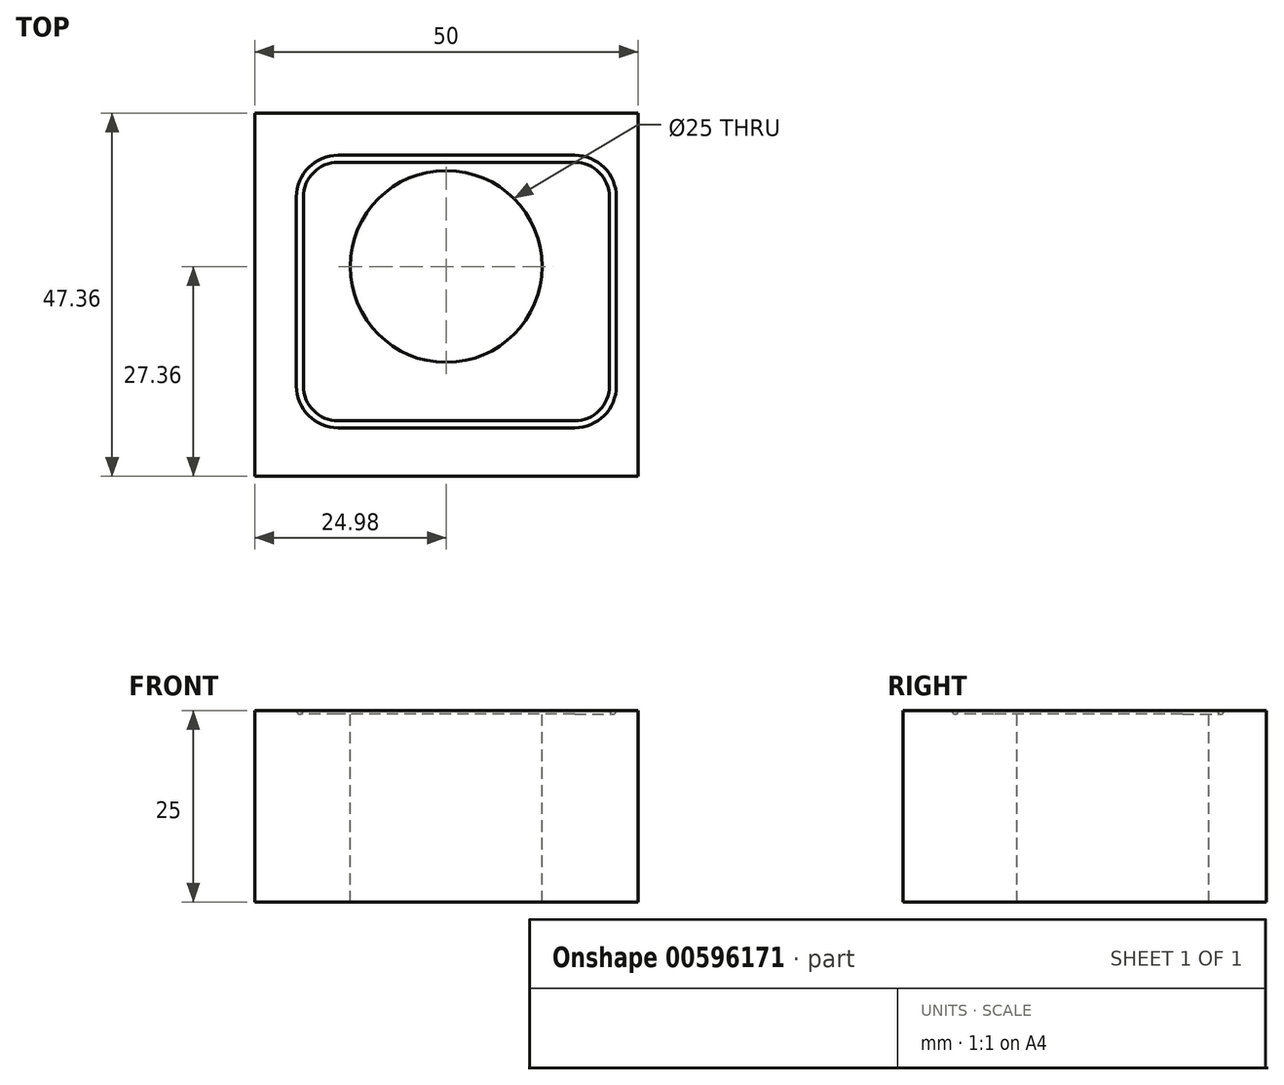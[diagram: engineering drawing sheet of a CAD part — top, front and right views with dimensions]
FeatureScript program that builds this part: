
annotation { "Feature Type Name" : "Feature", "Feature Type Description" : "" }
export const myFeature = defineFeature(function(context is Context, id is Id, definition is map)
    precondition{}
    {
        {
            var Q0;
            Q0=qCreatedBy(makeId("Top.planeOp"),FACE);
            var sketch = newSketch(context, id + "F0", { "sketchPlane" : qUnion([Q0])});
            skLineSegment(sketch, "E0.bottom", {"start": v(-24.98, 20) * mm, "end": v(25.02, 20) * mm});
            skLineSegment(sketch, "E0.top", {"start": v(-24.98, -27.36) * mm, "end": v(25.02, -27.36) * mm});
            skLineSegment(sketch, "E0.left", {"start": v(-24.98, 20) * mm, "end": v(-24.98, -27.36) * mm});
            skLineSegment(sketch, "E0.right", {"start": v(25.02, 20) * mm, "end": v(25.02, -27.36) * mm});
            skSolve(sketch);
        }
        {
            var Q0;
            Q0=makeQuery(id+"F0.imprint","IMPRINT",FACE,{"disambiguationData":[TD([[makeQuery(id+"F0.imprint","IMPRINT",EDGE,{"derivedFrom":sQuery(id+"F0.wireOp",EDGE,"E0.bottom")}),-1.0]])]});
            var Q1;
            Q1 = qBodyType(qCreatedBy(id + "F0" ,EDGE), BodyType.WIRE);
            var Q2;
            Q2=sQuery(id+"F0.wireOp",EDGE,"E0.right");
            extrude(context, id + "F1", {"entities" : qUnion([Q0]), "surfaceEntities" : qUnion([Q1, Q2]), "depth" : 25 * mm, "offsetDistance" : 25 * mm});
        }
        {
            var Q0;
            Q0=makeQuery(id+"F1.opExtrude","CAP_FACE",FACE,{"disambiguationData":[OSD([sQuery(id+"F0.wireOp",EDGE,"E0.bottom"),sQuery(id+"F0.wireOp",EDGE,"E0.top"),sQuery(id+"F0.wireOp",EDGE,"E0.left"),sQuery(id+"F0.wireOp",EDGE,"E0.right")])],"isStart":false});
            var sketch = newSketch(context, id + "F2", { "sketchPlane" : qUnion([Q0])});
            skCircle(sketch, "E1", {"center": v(0, 0) * mm, "radius": 12.5 * mm});
            skSolve(sketch);
        }
        {
            var Q0;
            Q0=makeQuery(id+"F2.imprint","IMPRINT",FACE,{"disambiguationData":[TD([[makeQuery(id+"F2.imprint","IMPRINT",EDGE,{"derivedFrom":sQuery(id+"F2.wireOp",EDGE,"E1")}),1.0]])]});
            var Q1;
            Q1=sQuery(id+"F2.wireOp",EDGE,"E1");
            extrude(context, id + "F3", {"entities" : qUnion([Q0]), "operationType" : NewBodyOperationType.REMOVE, "surfaceEntities" : qUnion([Q1]), "endBound" : BoundingType.UP_TO_NEXT, "oppositeDirection" : true, "depth" : 25 * mm, "offsetDistance" : 25 * mm});
        }
        {
            var Q0;
            Q0=makeQuery(id+"F1.opExtrude","CAP_FACE",FACE,{"disambiguationData":[OSD([sQuery(id+"F0.wireOp",EDGE,"E0.bottom"),sQuery(id+"F0.wireOp",EDGE,"E0.top"),sQuery(id+"F0.wireOp",EDGE,"E0.left"),sQuery(id+"F0.wireOp",EDGE,"E0.right")])],"isStart":false});
            var sketch = newSketch(context, id + "F4", { "sketchPlane" : qUnion([Q0])});
            skLineSegment(sketch, "E2.bottom", {"start": v(-14.07, 14.05) * mm, "end": v(16.75, 14.05) * mm});
            skLineSegment(sketch, "E2.top", {"start": v(-14.07, -20.59) * mm, "end": v(16.75, -20.59) * mm});
            skLineSegment(sketch, "E2.left", {"start": v(-19.07, 9.05) * mm, "end": v(-19.07, -15.59) * mm});
            skLineSegment(sketch, "E2.right", {"start": v(21.75, 9.05) * mm, "end": v(21.75, -15.59) * mm});
            skPoint(sketch, "E3.visualSharp", {"position": v(-19.07, 14.05) * mm});
            skArc(sketch, "E3.filletArc", {"start": v(-14.07, 14.05) * mm, "mid": v(-17.6, 12.59) * mm, "end": v(-19.07, 9.05) * mm});
            skPoint(sketch, "E4.visualSharp", {"position": v(21.75, 14.05) * mm});
            skArc(sketch, "E4.filletArc", {"start": v(21.75, 9.05) * mm, "mid": v(20.28, 12.59) * mm, "end": v(16.75, 14.05) * mm});
            skPoint(sketch, "E5.visualSharp", {"position": v(21.75, -20.59) * mm});
            skArc(sketch, "E5.filletArc", {"start": v(16.75, -20.59) * mm, "mid": v(20.28, -19.12) * mm, "end": v(21.75, -15.59) * mm});
            skPoint(sketch, "E6.visualSharp", {"position": v(-19.07, -20.59) * mm});
            skArc(sketch, "E6.filletArc", {"start": v(-19.07, -15.59) * mm, "mid": v(-17.6, -19.12) * mm, "end": v(-14.07, -20.59) * mm});
            skSolve(sketch);
        }
        {
            var Q0;
            Q0=qCreatedBy(makeId("Right.planeOp"),FACE);
            var sketch = newSketch(context, id + "F5", { "sketchPlane" : qUnion([Q0])});
            skCircle(sketch, "E7", {"center": v(-20.58, 25) * mm, "radius": 0.46 * mm});
            skSolve(sketch);
        }
        {
            var Q0;
            Q0=makeQuery(id+"F5.imprint","IMPRINT",FACE,{"disambiguationData":[TD([[makeQuery(id+"F5.imprint","IMPRINT",EDGE,{"derivedFrom":sQuery(id+"F5.wireOp",EDGE,"E7")}),1.0]])]});
            var Q1;
            Q1=sQuery(id+"F4.wireOp",EDGE,"E2.top");
            var Q2;
            Q2=sQuery(id+"F4.wireOp",EDGE,"E6.filletArc");
            var Q3;
            Q3=sQuery(id+"F4.wireOp",EDGE,"E2.left");
            var Q4;
            Q4=sQuery(id+"F4.wireOp",EDGE,"E3.filletArc");
            var Q5;
            Q5=sQuery(id+"F4.wireOp",EDGE,"E2.bottom");
            var Q6;
            Q6=sQuery(id+"F4.wireOp",EDGE,"E2.right");
            var Q7;
            Q7=sQuery(id+"F4.wireOp",EDGE,"E5.filletArc");
            var Q8;
            Q8=sQuery(id+"F4.wireOp",EDGE,"E4.filletArc");
            sweep(context, id + "F6", {"operationType" : NewBodyOperationType.REMOVE, "profiles" : qUnion([Q0]), "path" : qUnion([Q1, Q2, Q3, Q4, Q5, Q6, Q7, Q8])});
        }
    });
